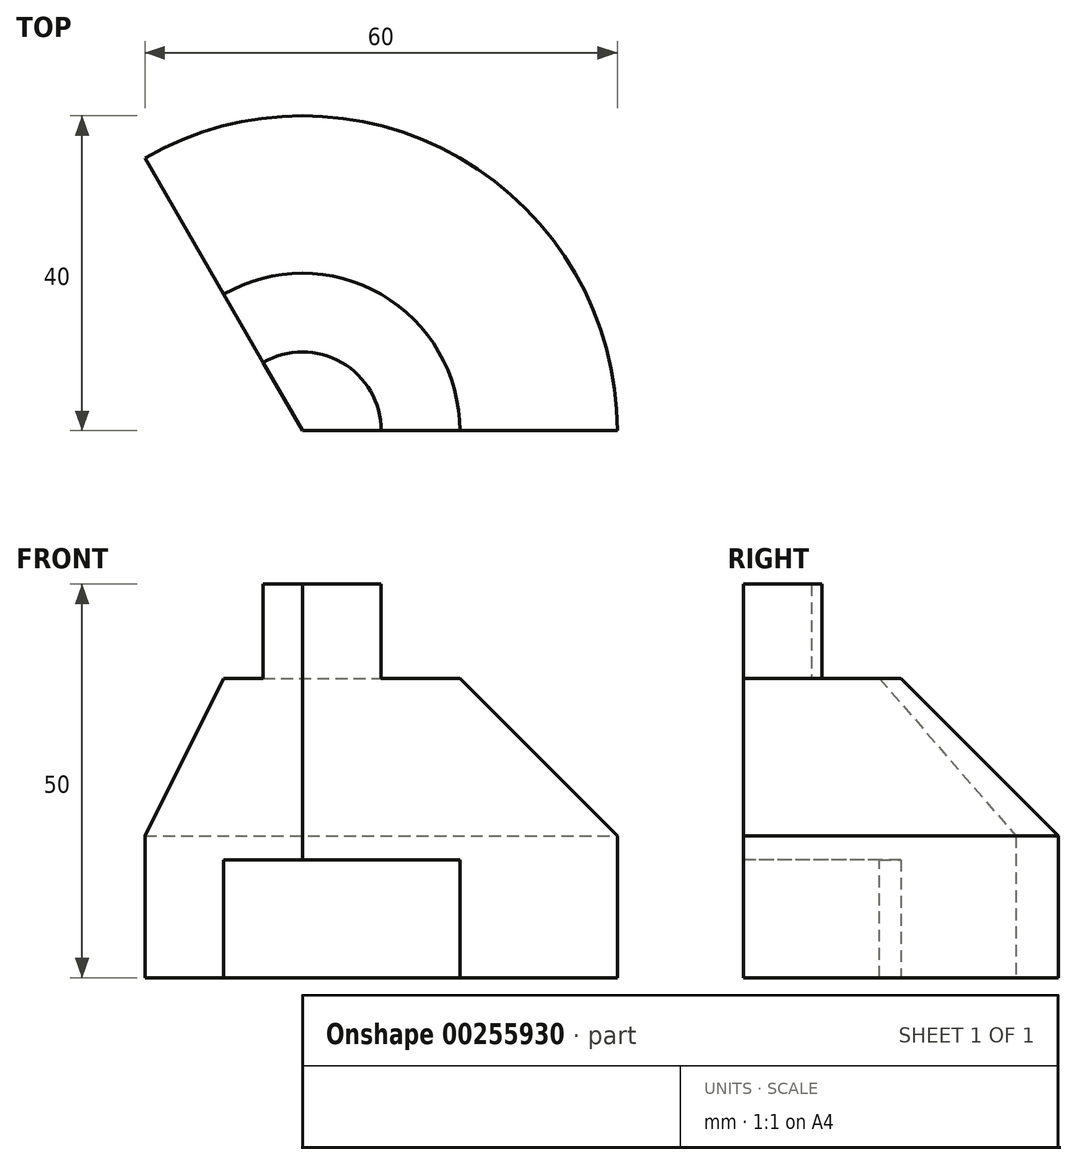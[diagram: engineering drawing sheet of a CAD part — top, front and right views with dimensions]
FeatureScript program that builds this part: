
annotation { "Feature Type Name" : "Feature", "Feature Type Description" : "" }
export const myFeature = defineFeature(function(context is Context, id is Id, definition is map)
    precondition{}
    {
        {
            var Q0;
            Q0=qCreatedBy(makeId("Front.planeOp"),FACE);
            var sketch = newSketch(context, id + "F0", { "sketchPlane" : qUnion([Q0])});
            skLineSegment(sketch, "E0", {"start": v(0, 0) * mm, "end": v(0, 35) * mm});
            skLineSegment(sketch, "E1", {"start": v(0, 35) * mm, "end": v(10, 35) * mm});
            skLineSegment(sketch, "E2", {"start": v(10, 35) * mm, "end": v(10, 23) * mm});
            skLineSegment(sketch, "E3", {"start": v(10, 23) * mm, "end": v(20, 23) * mm});
            skLineSegment(sketch, "E4", {"start": v(20, 23) * mm, "end": v(40, 3) * mm});
            skLineSegment(sketch, "E5", {"start": v(40, 3) * mm, "end": v(40, -15) * mm});
            skLineSegment(sketch, "E6", {"start": v(40, -15) * mm, "end": v(20, -15) * mm});
            skLineSegment(sketch, "E7", {"start": v(20, -15) * mm, "end": v(20, 0) * mm});
            skLineSegment(sketch, "E8", {"start": v(20, 0) * mm, "end": v(0, 0) * mm});
            skSolve(sketch);
        }
        {
            var Q0;
            Q0=makeQuery(id+"F0.imprint","IMPRINT",FACE,{"disambiguationData":[TD([[makeQuery(id+"F0.imprint","IMPRINT",EDGE,{"derivedFrom":sQuery(id+"F0.wireOp",EDGE,"E0")}),-1.0]])]});
            var Q1;
            Q1=sQuery(id+"F0.wireOp",EDGE,"E0");
            revolve(context, id + "F1", {"entities" : qUnion([Q0]), "axis" : qUnion([Q1]), "revolveType" : RevolveType.ONE_DIRECTION, "angle" : 120 * degree});
        }
    });
